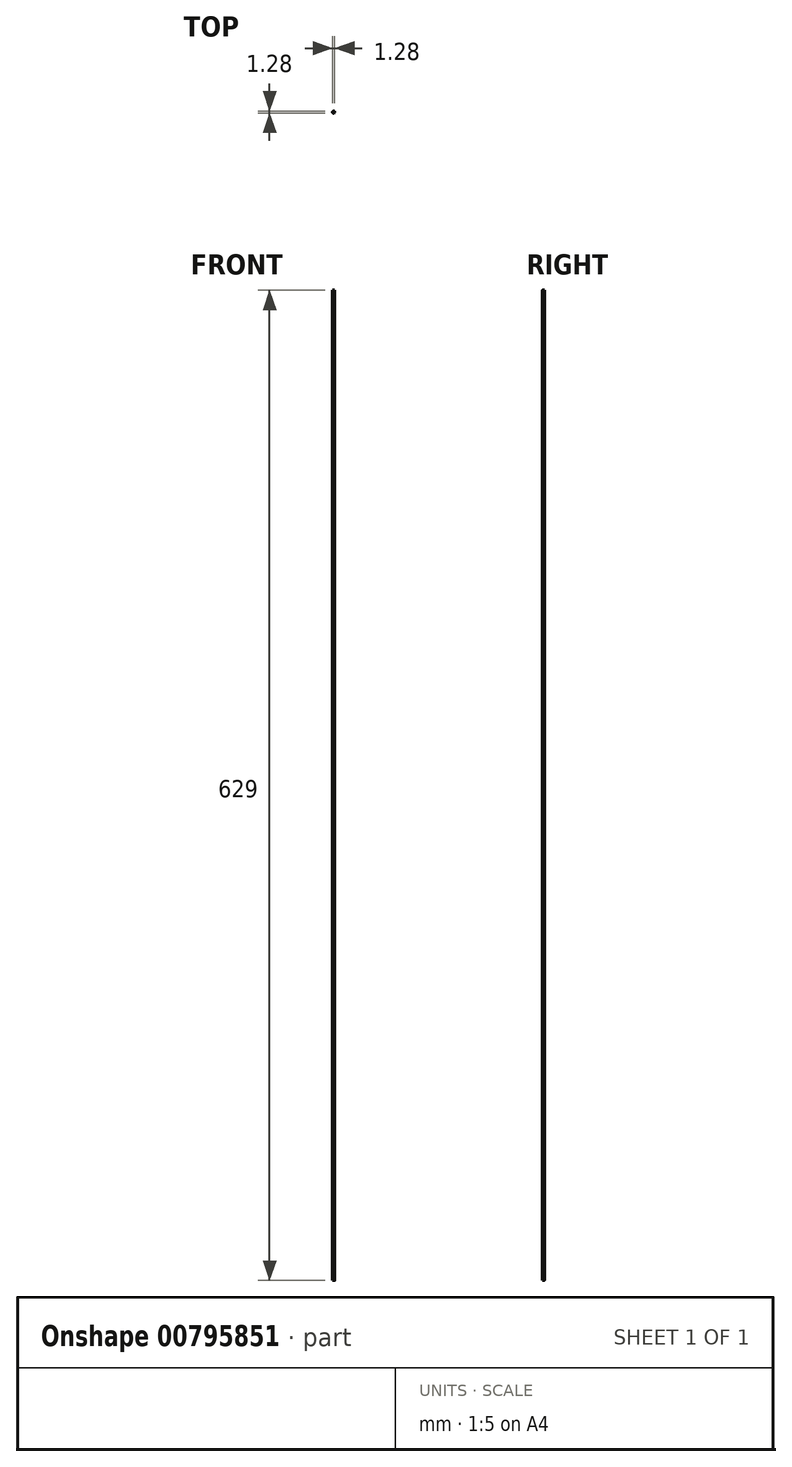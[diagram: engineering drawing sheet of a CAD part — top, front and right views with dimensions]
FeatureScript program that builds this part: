
annotation { "Feature Type Name" : "Feature", "Feature Type Description" : "" }
export const myFeature = defineFeature(function(context is Context, id is Id, definition is map)
    precondition{}
    {
        {
            var Q0;
            Q0=qCreatedBy(makeId("Top.planeOp"),FACE);
            var sketch = newSketch(context, id + "F0", { "sketchPlane" : qUnion([Q0])});
            skCircle(sketch, "E0", {"center": v(0, 0) * mm, "radius": 0.64 * mm});
            skSolve(sketch);
        }
        {
            var Q0;
            Q0 = qSketchRegion(id + "F0", true);
            extrude(context, id + "F1", {"entities" : qUnion([Q0]), "depth" : 629 * mm, "offsetDistance" : 25 * mm});
        }
    });
